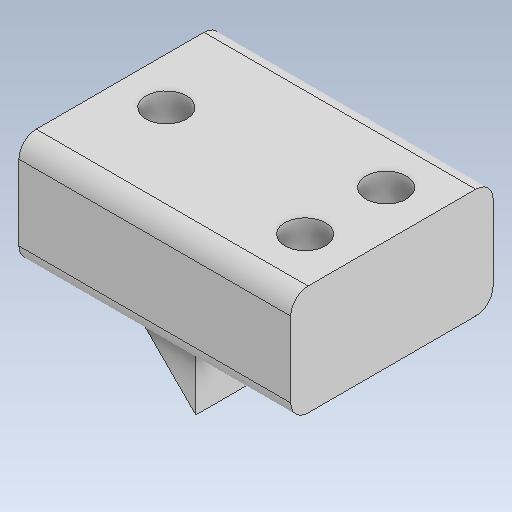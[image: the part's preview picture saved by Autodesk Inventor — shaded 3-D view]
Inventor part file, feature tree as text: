
AUTODESK INVENTOR PART (.ipt)
format: ipt  version: 2020.2 (Build 242310000, 310)  size: 184,320 bytes
history: native  units: mm
features: fillet x5, sketch x4, extrude x3, hole x2
ambient origin geometry x8: Origin, YZ Plane, XZ Plane, XY Plane, X Axis, Y Axis, Z Axis, Center Point
bodies: Solido1 (feature_tree)
feature tree (14):
  extrude  "Estrusione1"  Depth=35.0mm
  hole  "Foro1"  [1 undecoded]
  fillet  "Raccordo1"  Radius=19.0mm
  fillet  "Raccordo2"  Radius=8.0mm
  fillet  "Raccordo3"  [1 undecoded]
  fillet  "Raccordo4"  Radius=3.0mm
  hole  "Foro2"  [1 undecoded]
  extrude  "Estrusione2"  Depth=3.0mm
  extrude  "Estrusione3"  Depth=3.0mm
  fillet  "Raccordo5"  Radius=7.0mm
  sketch  "Schizzo1"
  sketch  "Schizzo3"
  sketch  "Schizzo4"
  sketch  "Schizzo5"
note: 3 required parameter values undecoded (feature->parameter linkage not recoverable at this tier; creation-order binding heuristic only, values carry confidence <= 0.55)
